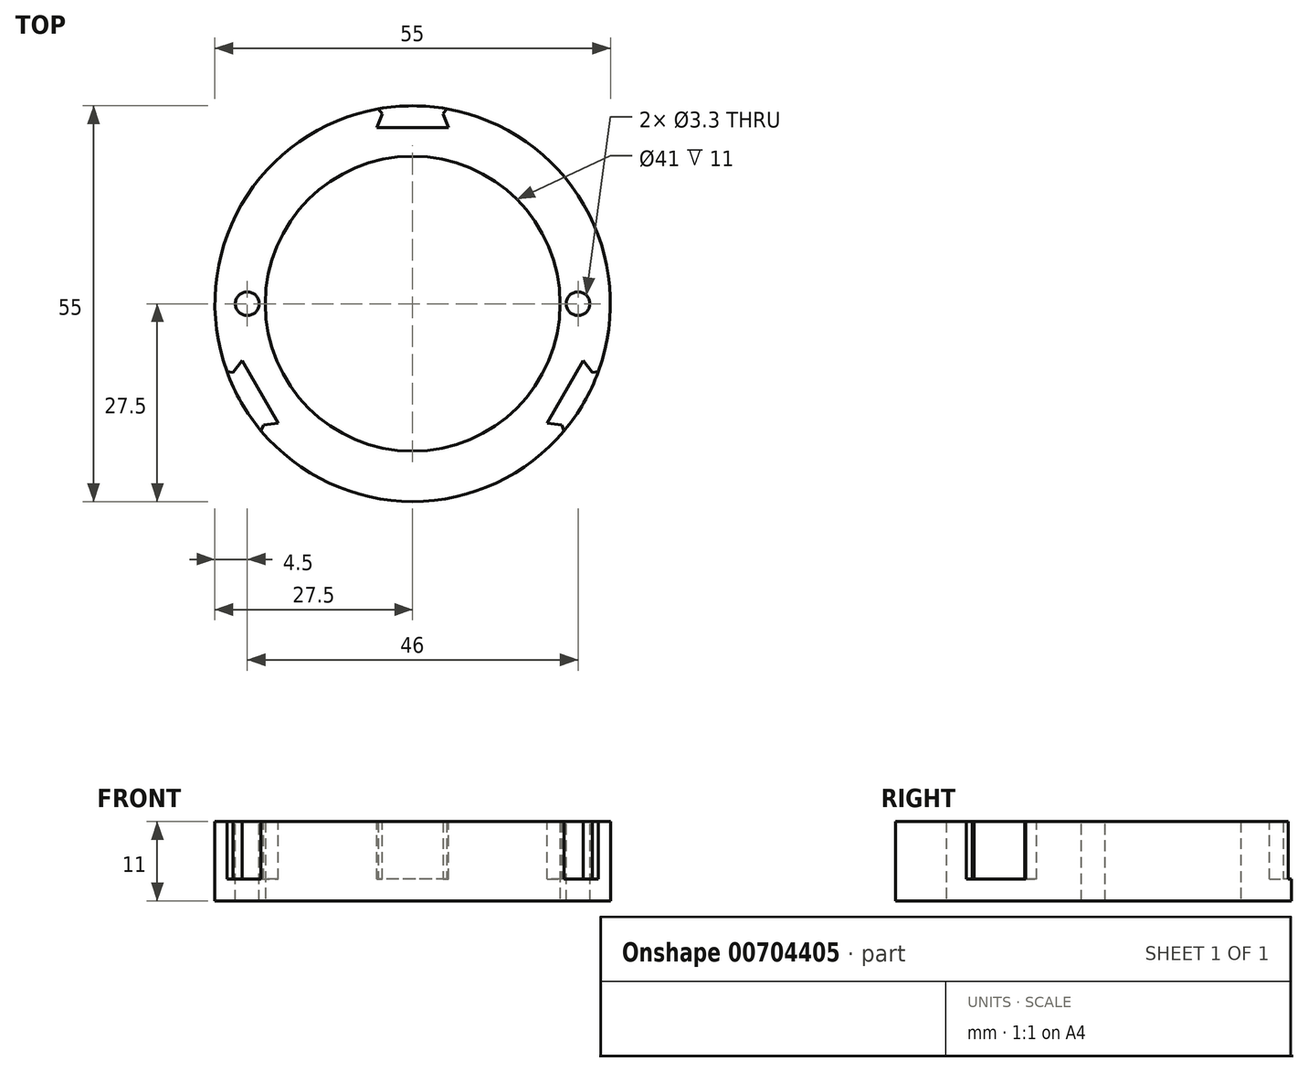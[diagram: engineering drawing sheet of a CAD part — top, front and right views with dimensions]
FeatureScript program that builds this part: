
annotation { "Feature Type Name" : "Feature", "Feature Type Description" : "" }
export const myFeature = defineFeature(function(context is Context, id is Id, definition is map)
    precondition{}
    {
        {
            var Q0;
            Q0=qCreatedBy(makeId("Top.planeOp"),FACE);
            var sketch = newSketch(context, id + "F0", { "sketchPlane" : qUnion([Q0])});
            skCircle(sketch, "E0", {"center": v(0, 0) * mm, "radius": 27.5 * mm});
            skCircle(sketch, "E1", {"center": v(0, 0) * mm, "radius": 20.5 * mm});
            skSolve(sketch);
        }
        {
            var Q0;
            Q0=makeQuery(id+"F0.imprint","IMPRINT",FACE,{"disambiguationData":[TD([[makeQuery(id+"F0.imprint","IMPRINT",EDGE,{"derivedFrom":sQuery(id+"F0.wireOp",EDGE,"E0")}),1.0]])]});
            extrude(context, id + "F1", {"entities" : qUnion([Q0]), "depth" : 11 * mm, "offsetDistance" : 25 * mm});
        }
        {
            var Q0;
            Q0=makeQuery(id+"F1.opExtrude","CAP_FACE",FACE,{"disambiguationData":[OSD([sQuery(id+"F0.wireOp",EDGE,"E0"),sQuery(id+"F0.wireOp",EDGE,"E1")])],"isStart":false});
            var sketch = newSketch(context, id + "F2", { "sketchPlane" : qUnion([Q0])});
            skCircle(sketch, "E2", {"center": v(-23, 0) * mm, "radius": 1.65 * mm});
            skCircle(sketch, "E3", {"center": v(23, 0) * mm, "radius": 1.65 * mm});
            skSolve(sketch);
        }
        {
            var Q0;
            Q0 = qSketchRegion(id + "F2", true);
            extrude(context, id + "F3", {"entities" : qUnion([Q0]), "operationType" : NewBodyOperationType.REMOVE, "endBound" : BoundingType.THROUGH_ALL, "oppositeDirection" : true, "depth" : 25 * mm, "offsetDistance" : 25 * mm});
        }
        {
            var Q0;
            Q0=makeQuery(id+"F1.opExtrude","CAP_FACE",FACE,{"disambiguationData":[OSD([sQuery(id+"F0.wireOp",EDGE,"E0"),sQuery(id+"F0.wireOp",EDGE,"E1")])],"isStart":false});
            var sketch = newSketch(context, id + "F4", { "sketchPlane" : qUnion([Q0])});
            skLineSegment(sketch, "E4", {"start": v(-2.5, 30.5) * mm, "end": v(2.5, 30.5) * mm});
            skLineSegment(sketch, "E5", {"start": v(2.5, 30.5) * mm, "end": v(5, 24.5) * mm});
            skLineSegment(sketch, "E6", {"start": v(5, 24.5) * mm, "end": v(-5, 24.5) * mm});
            skLineSegment(sketch, "E7", {"start": v(-5, 24.5) * mm, "end": v(-2.5, 30.5) * mm});
            skLineSegment(sketch, "E8.1.0", {"start": v(-25.16, -17.42) * mm, "end": v(-27.66, -13.08) * mm});
            skLineSegment(sketch, "E8.1.1", {"start": v(-18.72, -16.58) * mm, "end": v(-25.16, -17.42) * mm});
            skLineSegment(sketch, "E8.1.2", {"start": v(-27.66, -13.08) * mm, "end": v(-23.72, -7.92) * mm});
            skLineSegment(sketch, "E8.1.3", {"start": v(-23.72, -7.92) * mm, "end": v(-18.72, -16.58) * mm});
            skLineSegment(sketch, "E8.2.0", {"start": v(27.66, -13.08) * mm, "end": v(25.16, -17.42) * mm});
            skLineSegment(sketch, "E8.2.1", {"start": v(23.72, -7.92) * mm, "end": v(27.66, -13.08) * mm});
            skLineSegment(sketch, "E8.2.2", {"start": v(25.16, -17.42) * mm, "end": v(18.72, -16.58) * mm});
            skLineSegment(sketch, "E8.2.3", {"start": v(18.72, -16.58) * mm, "end": v(23.72, -7.92) * mm});
            skPoint(sketch, "E8.center", {"position": v(0, 0) * mm});
            skSolve(sketch);
        }
        {
            var Q0;
            Q0 = qSketchRegion(id + "F4", true);
            extrude(context, id + "F5", {"entities" : qUnion([Q0]), "operationType" : NewBodyOperationType.REMOVE, "oppositeDirection" : true, "depth" : 8 * mm, "offsetDistance" : 25 * mm});
        }
        {
            var Q0;
            Q0=makeQuery(id+"F5.boolean.opBoolean","INTERSECT",EDGE,{"derivedFrom":[makeQuery(id+"F1.opExtrude","SWEPT_FACE",FACE,{"disambiguationData":[OSD([sQuery(id+"F0.wireOp",EDGE,"E0")])]}),makeQuery(id+"F5.opExtrude","SWEPT_FACE",FACE,{"disambiguationData":[OSD([sQuery(id+"F4.wireOp",EDGE,"E5")])]})]});
            var Q1;
            Q1=makeQuery(id+"F5.boolean.opBoolean","INTERSECT",EDGE,{"derivedFrom":[makeQuery(id+"F1.opExtrude","SWEPT_FACE",FACE,{"disambiguationData":[OSD([sQuery(id+"F0.wireOp",EDGE,"E0")])]}),makeQuery(id+"F5.opExtrude","SWEPT_FACE",FACE,{"disambiguationData":[OSD([sQuery(id+"F4.wireOp",EDGE,"E7")])]})]});
            var Q2;
            Q2=makeQuery(id+"F5.boolean.opBoolean","INTERSECT",EDGE,{"derivedFrom":[makeQuery(id+"F1.opExtrude","SWEPT_FACE",FACE,{"disambiguationData":[OSD([sQuery(id+"F0.wireOp",EDGE,"E0")])]}),makeQuery(id+"F5.opExtrude","SWEPT_FACE",FACE,{"disambiguationData":[OSD([sQuery(id+"F4.wireOp",EDGE,"E8.2.1")])]})]});
            var Q3;
            Q3=makeQuery(id+"F5.boolean.opBoolean","INTERSECT",EDGE,{"derivedFrom":[makeQuery(id+"F1.opExtrude","SWEPT_FACE",FACE,{"disambiguationData":[OSD([sQuery(id+"F0.wireOp",EDGE,"E0")])]}),makeQuery(id+"F5.opExtrude","SWEPT_FACE",FACE,{"disambiguationData":[OSD([sQuery(id+"F4.wireOp",EDGE,"E8.2.2")])]})]});
            var Q4;
            Q4=makeQuery(id+"F5.boolean.opBoolean","INTERSECT",EDGE,{"derivedFrom":[makeQuery(id+"F1.opExtrude","SWEPT_FACE",FACE,{"disambiguationData":[OSD([sQuery(id+"F0.wireOp",EDGE,"E0")])]}),makeQuery(id+"F5.opExtrude","SWEPT_FACE",FACE,{"disambiguationData":[OSD([sQuery(id+"F4.wireOp",EDGE,"E8.1.2")])]})]});
            var Q5;
            Q5=makeQuery(id+"F5.boolean.opBoolean","INTERSECT",EDGE,{"derivedFrom":[makeQuery(id+"F1.opExtrude","SWEPT_FACE",FACE,{"disambiguationData":[OSD([sQuery(id+"F0.wireOp",EDGE,"E0")])]}),makeQuery(id+"F5.opExtrude","SWEPT_FACE",FACE,{"disambiguationData":[OSD([sQuery(id+"F4.wireOp",EDGE,"E8.1.1")])]})]});
            chamfer(context, id + "F6", {"entities" : qUnion([Q0, Q1, Q2, Q3, Q4, Q5]), "width" : 0.5 * mm, "tangentPropagation" : true});
        }
    });
